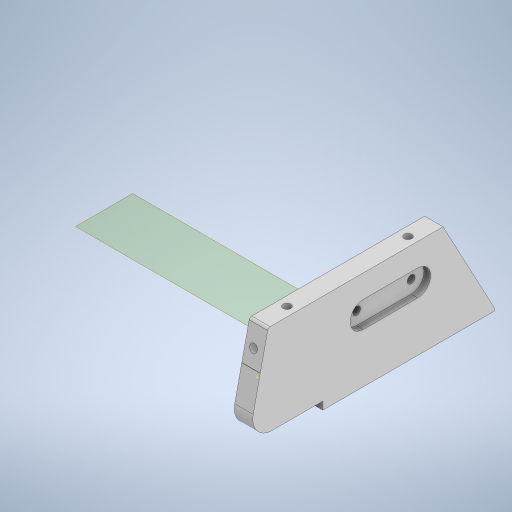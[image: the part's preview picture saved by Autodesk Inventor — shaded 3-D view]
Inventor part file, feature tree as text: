
AUTODESK INVENTOR PART (.ipt)
format: ipt  version: 2023 (Build 270158000, 158)  size: 638,976 bytes
history: native  units: mm
features: extrude x25, sketch x25, other x12, reference x10, projected_geometry x9, fillet x8, chamfer x1
ambient origin geometry x8: Origin, YZ Plane, XZ Plane, XY Plane, X Axis, Y Axis, Z Axis, Center Point
bodies: Body1 (feature_tree)
feature tree (90):
  other  "Bryła1"
  extrude  "Wyciągnięcie proste1"  Depth=6.5mm TaperAngle=0.0deg
  extrude  "Wyciągnięcie proste2"  Depth=3.7mm TaperAngle=0.0deg
  extrude  "Wyciągnięcie proste3"  Depth=1.5mm TaperAngle=0.0deg
  extrude  "Wyciągnięcie proste4"  Depth=6.0mm
  extrude  "Wyciągnięcie proste5"  Depth=3.0mm TaperAngle=0.0deg
  extrude  "Wyciągnięcie proste6"  Depth=5.0mm
  extrude  "Wyciągnięcie proste7"  Depth=3.0mm
  fillet  "Zaokrąglenie1"  Radius=15.0mm
  extrude  "Wyciągnięcie proste8"  Depth=6.0mm
  fillet  "Zaokrąglenie2"  Radius=15.0mm
  fillet  "Zaokrąglenie3"  Radius=35.5mm
  extrude  "Wyciągnięcie proste9"  TaperAngle=0.0deg  [1 undecoded]
  extrude  "Wyciągnięcie proste10"  Depth=5.0mm
  other  "Płaszczyzna konstrukcyjna1"
  extrude  "Wyciągnięcie proste11"  Depth=10.0mm TaperAngle=0.0deg
  extrude  "Wyciągnięcie proste12"  Depth=3.5mm
  extrude  "Wyciągnięcie proste13"  Depth=2.0mm
  other  "Płaszczyzna konstrukcyjna2"
  extrude  "Wyciągnięcie proste14"  Depth=7.22mm
  extrude  "Wyciągnięcie proste15"  Depth=3.0mm
  chamfer  "Faza1"  Distance=15.0mm
  fillet  "Zaokrąglenie7"  Radius=26.342mm
  fillet  "Zaokrąglenie8"  Radius=3.0mm
  fillet  "Zaokrąglenie9"  Radius=15.0mm
  extrude  "Wyciągnięcie proste16"  [1 undecoded]
  extrude  "Wyciągnięcie proste17"  Depth=5.7mm
  fillet  "Zaokrąglenie10"  Radius=4.0mm
  sketch  "Szkic18"
  other  "Płaszczyzna konstrukcyjna3"
  extrude  "Wyciągnięcie proste18"  Depth=10.0mm
  sketch  "Szkic19"
  extrude  "Wyciągnięcie proste19"  Depth=10.0mm
  extrude  "Wyciągnięcie proste20"  Depth=7.0mm TaperAngle=0.0deg
  fillet  "Zaokrąglenie11"  Radius=7.0mm
  extrude  "Wyciągnięcie proste21"  Depth=8.0mm
  extrude  "Wyciągnięcie proste22"  Depth=5.0mm TaperAngle=0.0deg
  extrude  "Wyciągnięcie proste23"  Depth=7.0mm
  sketch  "Szkic25"
  extrude  "Wyciągnięcie proste24"  Depth=0.5mm TaperAngle=0.0deg
  extrude  "Wyciągnięcie proste25"  Depth=0.5mm TaperAngle=45.0deg
  sketch  "Szkic1"
  sketch  "Szkic2"
  sketch  "Szkic3"
  sketch  "Szkic4"
  sketch  "Szkic5"
  sketch  "Szkic6"
  projected_geometry  "Pętla rzutowana1"
  sketch  "Szkic7"
  sketch  "Szkic8"
  projected_geometry  "Pętla rzutowana2"
  sketch  "Szkic9"
  sketch  "Szkic10"
  sketch  "Szkic11"
  sketch  "Szkic12"
  reference  "Odniesienie1"
  reference  "Odniesienie2"
  sketch  "Szkic13"
  sketch  "Szkic14"
  reference  "Odniesienie3"
  sketch  "Szkic15"
  projected_geometry  "Pętla rzutowana3"
  sketch  "Szkic16"
  projected_geometry  "Pętla rzutowana4"
  sketch  "Szkic17"
  reference  "Odniesienie4"
  reference  "Odniesienie5"
  reference  "Odniesienie6"
  reference  "Odniesienie7"
  projected_geometry  "Pętla rzutowana5"
  sketch  "Szkic20"
  projected_geometry  "Pętla rzutowana6"
  reference  "Odniesienie8"
  sketch  "Szkic21"
  projected_geometry  "Pętla rzutowana7"
  sketch  "Szkic22"
  projected_geometry  "Pętla rzutowana8"
  reference  "Odniesienie9"
  reference  "Odniesienie10"
  sketch  "Szkic23"
  sketch  "Szkic24"
  projected_geometry  "Pętla rzutowana9"
  other  "<userpath>\Desktop\MojeRoboty\Stefan\mechanics 2\STEFAN.iam"
  other  "STEFAN.iam"
  other  "plytka_dol:1"
  other  "ARDUINO_NANO:1"
  other  "board_up:1"
  other  "koło_minisumo:2"
  other  "podstawa:1"
  other  "plug_2:1"
note: 2 required parameter values undecoded (feature->parameter linkage not recoverable at this tier; creation-order binding heuristic only, values carry confidence <= 0.55)
